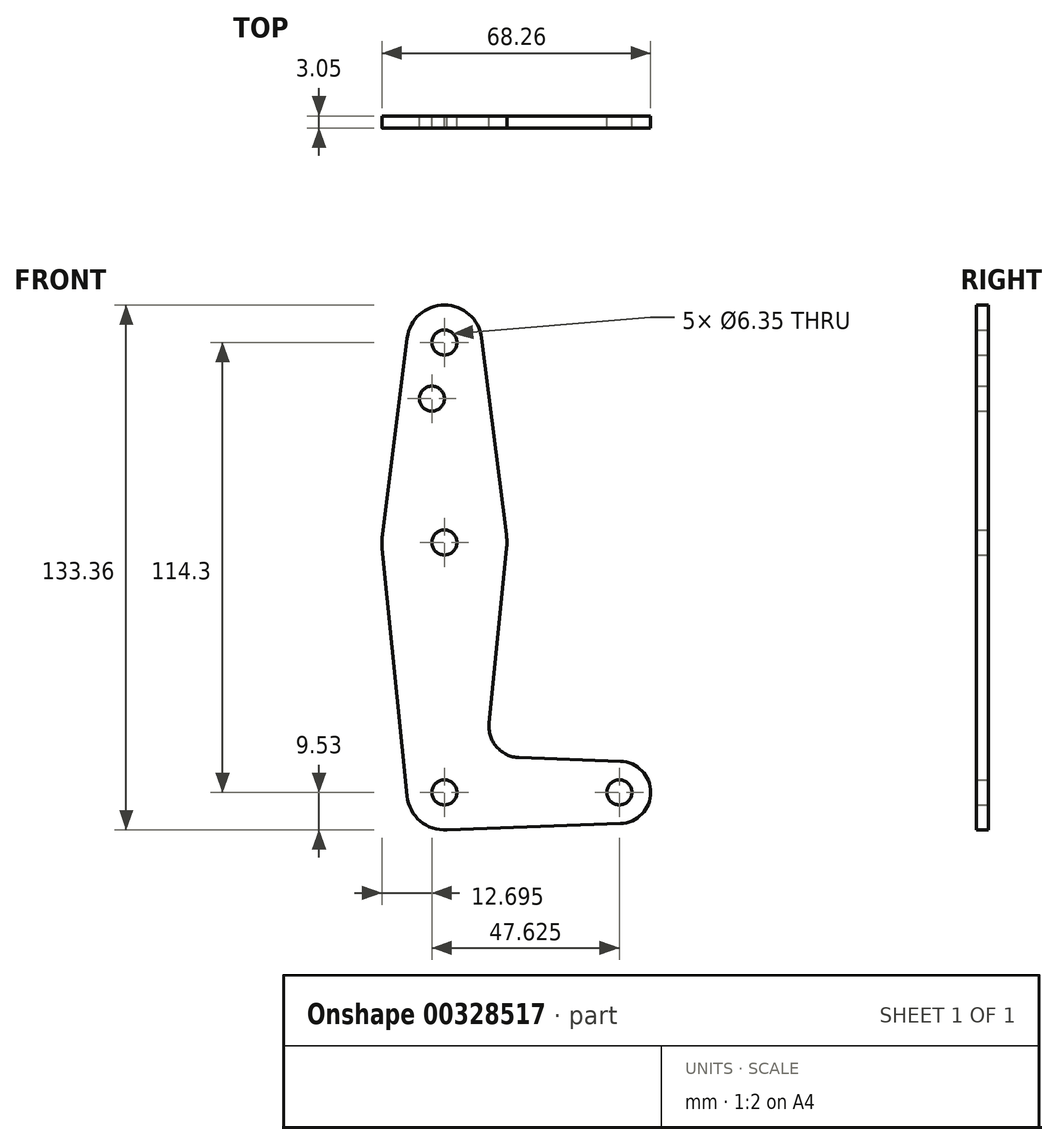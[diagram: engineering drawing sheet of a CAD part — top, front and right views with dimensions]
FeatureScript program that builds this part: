
annotation { "Feature Type Name" : "Feature", "Feature Type Description" : "" }
export const myFeature = defineFeature(function(context is Context, id is Id, definition is map)
    precondition{}
    {
        {
            var Q0;
            Q0=qCreatedBy(makeId("Front.planeOp"),FACE);
            var sketch = newSketch(context, id + "F0", { "sketchPlane" : qUnion([Q0])});
            skLineSegment(sketch, "E0", {"start": v(0, 0) * mm, "end": v(44.45, 0) * mm, "construction": true});
            skLineSegment(sketch, "E1", {"start": v(0, 0) * mm, "end": v(0, 114.3) * mm, "construction": true});
            skCircle(sketch, "E2", {"center": v(0, 114.3) * mm, "radius": 9.53 * mm});
            skCircle(sketch, "E3", {"center": v(0, 0) * mm, "radius": 9.53 * mm});
            skCircle(sketch, "E4", {"center": v(44.45, 0) * mm, "radius": 7.94 * mm});
            skLineSegment(sketch, "E5", {"start": v(-9.45, 115.5) * mm, "end": v(-15.75, 65.48) * mm});
            skLineSegment(sketch, "E6", {"start": v(9.45, 115.5) * mm, "end": v(15.75, 65.48) * mm});
            skLineSegment(sketch, "E7", {"start": v(18.97, 8.85) * mm, "end": v(44.73, 7.93) * mm});
            skLineSegment(sketch, "E8", {"start": v(0, -9.53) * mm, "end": v(44.73, -7.93) * mm});
            skCircle(sketch, "E9", {"center": v(0, 114.3) * mm, "radius": 3.18 * mm});
            skCircle(sketch, "E10", {"center": v(-3.18, 100.03) * mm, "radius": 3.18 * mm});
            skCircle(sketch, "E11", {"center": v(0, 63.5) * mm, "radius": 3.18 * mm});
            skCircle(sketch, "E12", {"center": v(0, 0) * mm, "radius": 3.18 * mm});
            skCircle(sketch, "E13", {"center": v(44.45, 0) * mm, "radius": 3.18 * mm});
            skCircle(sketch, "E14", {"center": v(0, 63.5) * mm, "radius": 15.88 * mm});
            skLineSegment(sketch, "E15", {"start": v(-15.8, 61.91) * mm, "end": v(-9.48, -0.95) * mm});
            skLineSegment(sketch, "E16", {"start": v(15.8, 61.91) * mm, "end": v(11.34, 17.59) * mm});
            skArc(sketch, "E17.filletArc", {"start": v(11.34, 17.59) * mm, "mid": v(13.26, 11.57) * mm, "end": v(18.97, 8.85) * mm});
            skSolve(sketch);
        }
        {
            var Q0;
            Q0 = qSketchRegion(id + "F0", true);
            extrude(context, id + "F1", {"entities" : qUnion([Q0]), "depth" : 3.05 * mm});
        }
    });
